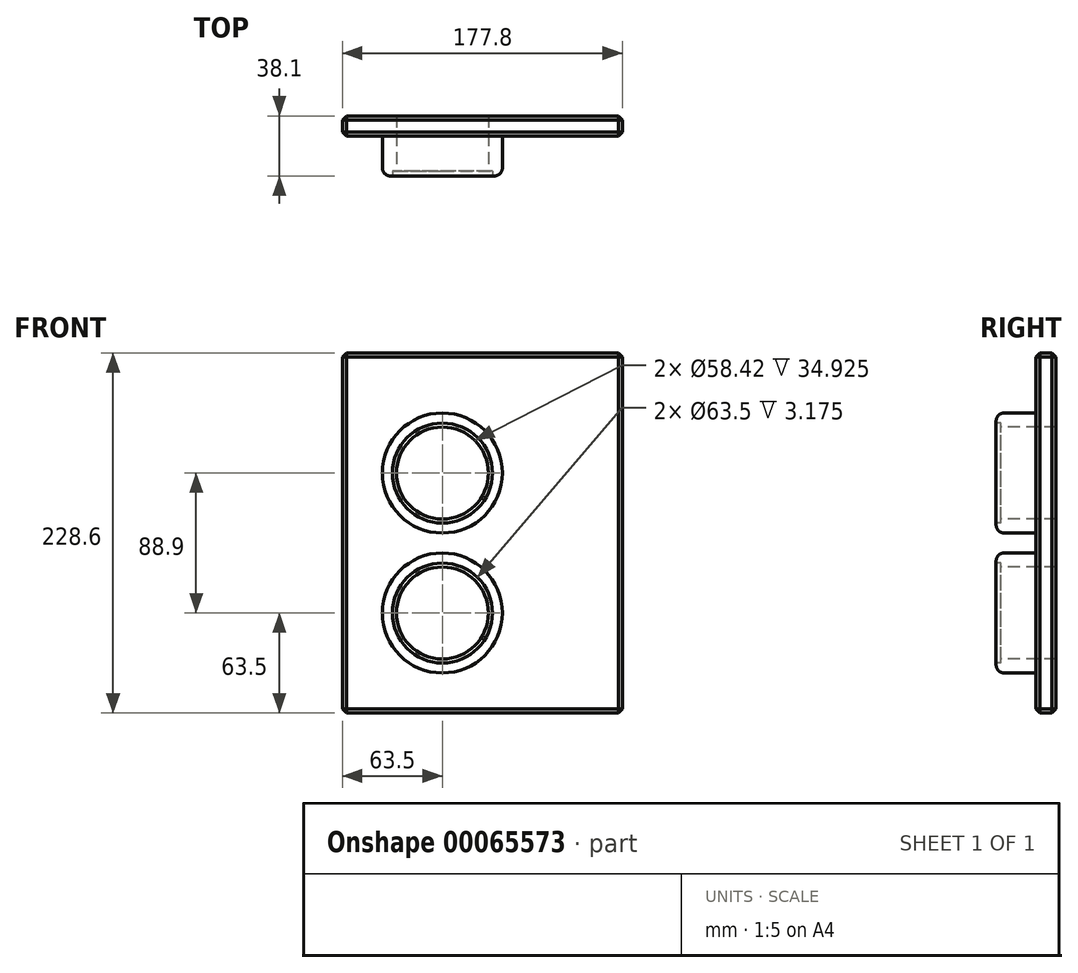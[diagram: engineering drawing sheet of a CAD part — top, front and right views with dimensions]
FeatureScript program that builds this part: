
annotation { "Feature Type Name" : "Feature", "Feature Type Description" : "" }
export const myFeature = defineFeature(function(context is Context, id is Id, definition is map)
    precondition{}
    {
        {
            var Q0;
            Q0=qCreatedBy(makeId("Front.planeOp"),FACE);
            var sketch = newSketch(context, id + "F0", { "sketchPlane" : qUnion([Q0])});
            skLineSegment(sketch, "E0.rect.bottom", {"start": v(0, 0) * mm, "end": v(0, 0) * mm});
            skLineSegment(sketch, "E0.rect.top", {"start": v(0, 0) * mm, "end": v(0, 0) * mm});
            skLineSegment(sketch, "E0.rect.left", {"start": v(0, 0) * mm, "end": v(0, 0) * mm});
            skLineSegment(sketch, "E0.rect.right", {"start": v(0, 0) * mm, "end": v(0, 0) * mm});
            skPoint(sketch, "E0.rect.middle", {"position": v(0, 0) * mm});
            skLineSegment(sketch, "E1.rect.bottom", {"start": v(0, 0) * mm, "end": v(177.8, 0) * mm});
            skLineSegment(sketch, "E1.rect.top", {"start": v(0, 228.6) * mm, "end": v(177.8, 228.6) * mm});
            skLineSegment(sketch, "E1.rect.left", {"start": v(0, 0) * mm, "end": v(0, 228.6) * mm});
            skPoint(sketch, "E1.rect.middle", {"position": v(88.9, 114.3) * mm});
            skLineSegment(sketch, "E2", {"start": v(177.8, 0) * mm, "end": v(177.8, 0) * mm});
            skLineSegment(sketch, "E3", {"start": v(177.8, 0) * mm, "end": v(177.8, 228.6) * mm});
            skPoint(sketch, "E4.start.orphan", {"position": v(177.8, 318.94) * mm});
            skSolve(sketch);
        }
        {
            var Q0;
            Q0 = qSketchRegion(id + "F0", true);
            extrude(context, id + "F1", {"entities" : qUnion([Q0]), "depth" : 12.7 * mm});
        }
        {
            var Q0;
            Q0=makeQuery(id+"F1.opExtrude","CAP_FACE",FACE,{"disambiguationData":[OSD([sQuery(id+"F0.wireOp",EDGE,"E1.rect.bottom"),sQuery(id+"F0.wireOp",EDGE,"E1.rect.top"),sQuery(id+"F0.wireOp",EDGE,"E1.rect.left"),sQuery(id+"F0.wireOp",EDGE,"E3")])],"isStart":false});
            var sketch = newSketch(context, id + "F2", { "sketchPlane" : qUnion([Q0])});
            skCircle(sketch, "E5", {"center": v(63.5, 152.4) * mm, "radius": 38.1 * mm});
            skCircle(sketch, "E6", {"center": v(63.5, 63.5) * mm, "radius": 38.1 * mm});
            skSolve(sketch);
        }
        {
            var Q0;
            Q0 = qSketchRegion(id + "F2", true);
            extrude(context, id + "F3", {"entities" : qUnion([Q0]), "operationType" : NewBodyOperationType.ADD, "depth" : 25.4 * mm});
        }
        {
            var Q0;
            Q0=makeQuery(id+"F1.opExtrude","CAP_EDGE",EDGE,{"disambiguationData":[OSD([sQuery(id+"F0.wireOp",EDGE,"E3")])],"isStart":false});
            var Q1;
            Q1=makeQuery(id+"F1.opExtrude","CAP_EDGE",EDGE,{"disambiguationData":[OSD([sQuery(id+"F0.wireOp",EDGE,"E3")])],"isStart":true});
            var Q2;
            Q2=makeQuery(id+"F1.opExtrude","CAP_EDGE",EDGE,{"disambiguationData":[OSD([sQuery(id+"F0.wireOp",EDGE,"E1.rect.top")])],"isStart":false});
            var Q3;
            Q3=makeQuery(id+"F1.opExtrude","CAP_EDGE",EDGE,{"disambiguationData":[OSD([sQuery(id+"F0.wireOp",EDGE,"E1.rect.top")])],"isStart":true});
            var Q4;
            Q4=makeQuery(id+"F1.opExtrude","CAP_EDGE",EDGE,{"disambiguationData":[OSD([sQuery(id+"F0.wireOp",EDGE,"E1.rect.left")])],"isStart":false});
            var Q5;
            Q5=makeQuery(id+"F1.opExtrude","CAP_EDGE",EDGE,{"disambiguationData":[OSD([sQuery(id+"F0.wireOp",EDGE,"E1.rect.left")])],"isStart":true});
            var Q6;
            Q6=makeQuery(id+"F1.opExtrude","CAP_EDGE",EDGE,{"disambiguationData":[OSD([sQuery(id+"F0.wireOp",EDGE,"E1.rect.bottom")])],"isStart":false});
            var Q7;
            Q7=makeQuery(id+"F1.opExtrude","CAP_EDGE",EDGE,{"disambiguationData":[OSD([sQuery(id+"F0.wireOp",EDGE,"E1.rect.bottom")])],"isStart":true});
            var Q8;
            Q8=makeQuery(id+"F1.opExtrude","SWEPT_EDGE",EDGE,{"disambiguationData":[OSD([sQuery(id+"F0.wireOp",EDGE,"E1.rect.bottom"),sQuery(id+"F0.wireOp",EDGE,"E1.rect.left")])]});
            var Q9;
            Q9=makeQuery(id+"F1.opExtrude","SWEPT_EDGE",EDGE,{"disambiguationData":[OSD([sQuery(id+"F0.wireOp",EDGE,"E1.rect.bottom"),sQuery(id+"F0.wireOp",EDGE,"E3")])]});
            var Q10;
            Q10=makeQuery(id+"F1.opExtrude","SWEPT_EDGE",EDGE,{"disambiguationData":[OSD([sQuery(id+"F0.wireOp",EDGE,"E1.rect.top"),sQuery(id+"F0.wireOp",EDGE,"E1.rect.left")])]});
            var Q11;
            Q11=makeQuery(id+"F1.opExtrude","CAP_FACE",FACE,{"disambiguationData":[OSD([sQuery(id+"F0.wireOp",EDGE,"E1.rect.bottom"),sQuery(id+"F0.wireOp",EDGE,"E1.rect.top"),sQuery(id+"F0.wireOp",EDGE,"E1.rect.left"),sQuery(id+"F0.wireOp",EDGE,"E3")])],"isStart":true});
            var Q12;
            Q12=makeQuery(id+"F1.opExtrude","SWEPT_EDGE",EDGE,{"disambiguationData":[OSD([sQuery(id+"F0.wireOp",EDGE,"E1.rect.top"),sQuery(id+"F0.wireOp",EDGE,"E3")])]});
            chamfer(context, id + "F4", {"entities" : qUnion([Q0, Q1, Q2, Q3, Q4, Q5, Q6, Q7, Q8, Q9, Q10, Q11, Q12]), "width" : 2.54 * mm, "tangentPropagation" : true});
        }
        {
            var Q0;
            Q0=makeQuery(id+"F3.opExtrude","CAP_EDGE",EDGE,{"disambiguationData":[OSD([sQuery(id+"F2.wireOp",EDGE,"E6")])],"isStart":false});
            var Q1;
            Q1=makeQuery(id+"F3.opExtrude","CAP_EDGE",EDGE,{"disambiguationData":[OSD([sQuery(id+"F2.wireOp",EDGE,"E5")])],"isStart":false});
            fillet(context, id + "F5", {"entities" : qUnion([Q0, Q1]), "radius" : 5.08 * mm, "tangentPropagation" : true, "allowEdgeOverflow" : false});
        }
        {
            var Q0;
            Q0=makeQuery(id+"F3.opExtrude","CAP_FACE",FACE,{"disambiguationData":[OSD([sQuery(id+"F2.wireOp",EDGE,"E5")])],"isStart":false});
            var sketch = newSketch(context, id + "F6", { "sketchPlane" : qUnion([Q0])});
            skPoint(sketch, "E7", {"position": v(63.5, 152.4) * mm});
            skPoint(sketch, "E8", {"position": v(63.5, 63.5) * mm});
            skSolve(sketch);
        }
        {
            var Q0;
            Q0=sQuery(id+"F6.wireOp",VERTEX,"E7");
            var Q1;
            Q1=sQuery(id+"F6.wireOp",VERTEX,"E8");
            var Q2;
            Q2=makeQuery(id+"F1.opExtrude","SWEPT_BODY",BODY,{"disambiguationData":[OSD([sQuery(id+"F0.wireOp",EDGE,"E1.rect.bottom"),sQuery(id+"F0.wireOp",EDGE,"E1.rect.top"),sQuery(id+"F0.wireOp",EDGE,"E1.rect.left"),sQuery(id+"F0.wireOp",EDGE,"E3")])]});
            hole(context, id + "F7", {"style" : HoleStyle.C_BORE, "holeDiameter" : 58.42 * mm, "cBoreDiameter" : 63.5 * mm, "cBoreDepth" : 3.17 * mm, "endStyle" : HoleEndStyle.THROUGH, "locations" : qUnion([Q0, Q1]), "scope" : qUnion([Q2])});
        }
    });
